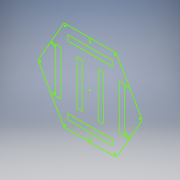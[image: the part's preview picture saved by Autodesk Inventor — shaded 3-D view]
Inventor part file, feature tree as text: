
AUTODESK INVENTOR PART (.ipt)
format: ipt  version: 2019 (Build 230136000, 136)  size: 107,520 bytes
history: native  units: mm
features: sketch x1
ambient origin geometry x8: Origin, YZ Plane, XZ Plane, XY Plane, X Axis, Y Axis, Z Axis, Center Point
feature tree (1):
  sketch  "Sketch1"
